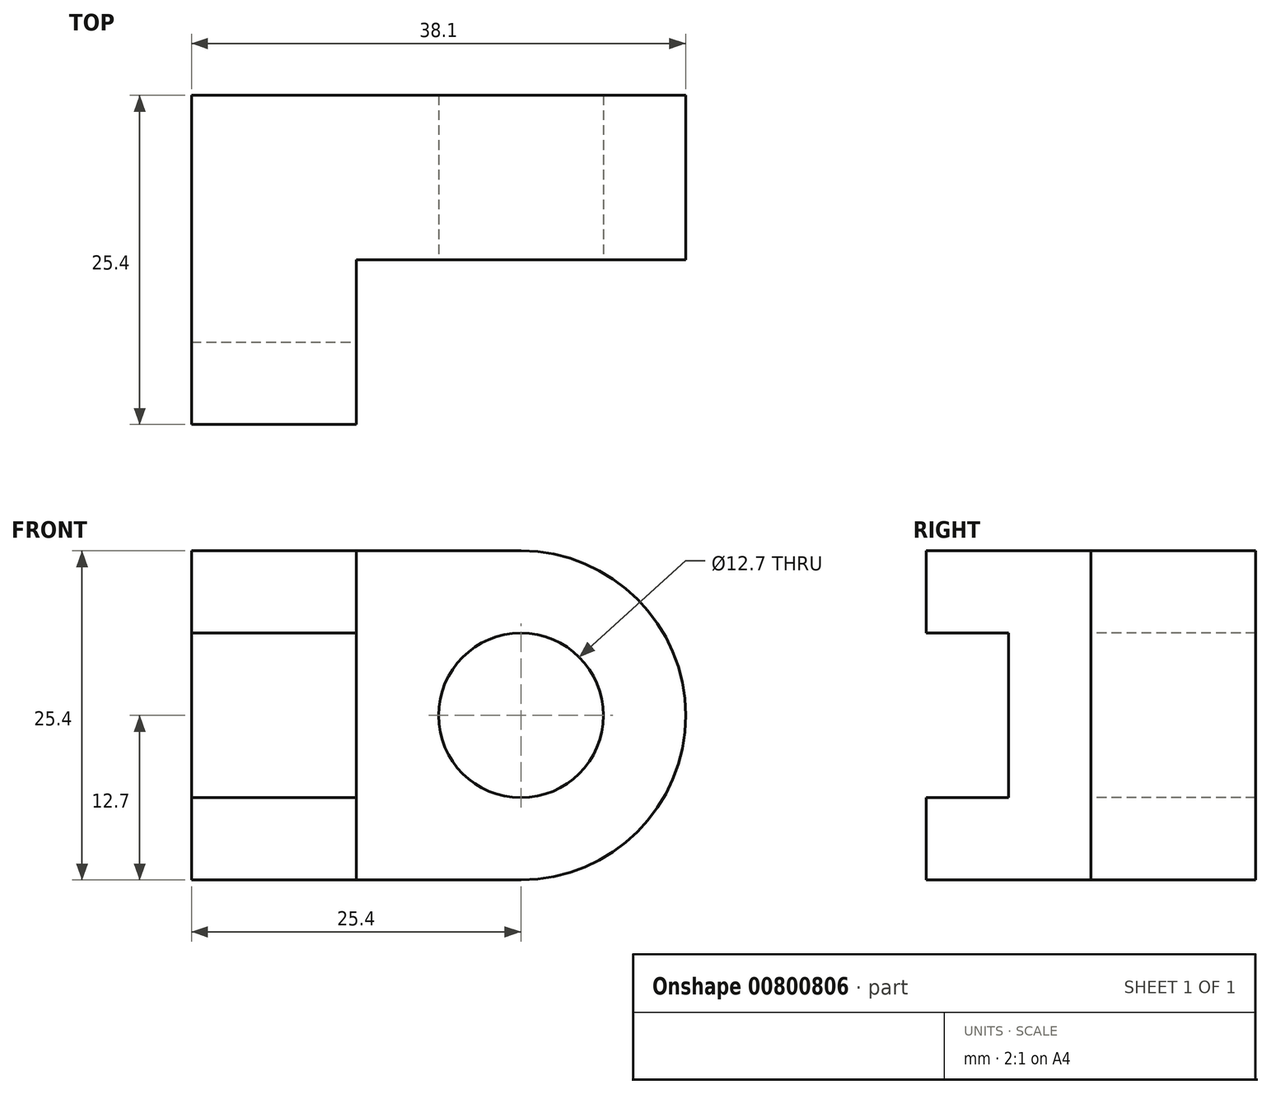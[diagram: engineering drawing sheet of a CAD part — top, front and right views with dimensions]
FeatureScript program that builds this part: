
annotation { "Feature Type Name" : "Feature", "Feature Type Description" : "" }
export const myFeature = defineFeature(function(context is Context, id is Id, definition is map)
    precondition{}
    {
        {
            var Q0;
            Q0=qCreatedBy(makeId("Top.planeOp"),FACE);
            var sketch = newSketch(context, id + "F0", { "sketchPlane" : qUnion([Q0])});
            skLineSegment(sketch, "E0", {"start": v(0, 0) * mm, "end": v(0, -25.4) * mm});
            skLineSegment(sketch, "E1", {"start": v(0, -25.4) * mm, "end": v(12.7, -25.4) * mm});
            skLineSegment(sketch, "E2", {"start": v(12.7, -25.4) * mm, "end": v(12.7, -12.7) * mm});
            skLineSegment(sketch, "E3", {"start": v(12.7, -12.7) * mm, "end": v(50.8, -12.7) * mm});
            skLineSegment(sketch, "E4", {"start": v(50.8, -12.7) * mm, "end": v(50.8, 0) * mm});
            skLineSegment(sketch, "E5", {"start": v(50.8, 0) * mm, "end": v(0, 0) * mm});
            skSolve(sketch);
        }
        {
            var Q0;
            Q0 = qSketchRegion(id + "F0", true);
            extrude(context, id + "F1", {"entities" : qUnion([Q0]), "oppositeDirection" : true, "depth" : 25.4 * mm, "offsetDistance" : 25.4 * mm});
        }
        {
            var Q0;
            Q0=makeQuery(id+"F1.opExtrude","SWEPT_FACE",FACE,{"disambiguationData":[OSD([sQuery(id+"F0.wireOp",EDGE,"E2")])]});
            var sketch = newSketch(context, id + "F2", { "sketchPlane" : qUnion([Q0])});
            skLineSegment(sketch, "E6", {"start": v(-25.4, 0) * mm, "end": v(-25.4, -6.35) * mm});
            skLineSegment(sketch, "E7", {"start": v(-25.4, -6.35) * mm, "end": v(-19.05, -6.35) * mm});
            skLineSegment(sketch, "E8", {"start": v(-19.05, -6.35) * mm, "end": v(-19.05, -19.05) * mm});
            skLineSegment(sketch, "E9", {"start": v(-19.05, -19.05) * mm, "end": v(-25.4, -19.05) * mm});
            skLineSegment(sketch, "E10", {"start": v(-25.4, -19.05) * mm, "end": v(-25.4, -25.4) * mm});
            skLineSegment(sketch, "E11", {"start": v(-25.4, -25.4) * mm, "end": v(-12.7, -25.4) * mm});
            skLineSegment(sketch, "E12", {"start": v(-12.7, -25.4) * mm, "end": v(-12.7, 0) * mm});
            skLineSegment(sketch, "E13", {"start": v(-12.7, 0) * mm, "end": v(-25.4, 0) * mm});
            skSolve(sketch);
        }
        {
            var Q0;
            {var subQ0=sQuery(id+"F2.wireOp",EDGE,"E7");Q0=makeQuery(id+"F2.imprint","IMPRINT",FACE,{"disambiguationData":[TD([[makeQuery(id+"F2.imprint","IMPRINT",EDGE,{"derivedFrom":subQ0}),-1.0]])]});}
            extrude(context, id + "F3", {"entities" : qUnion([Q0]), "operationType" : NewBodyOperationType.REMOVE, "oppositeDirection" : true, "depth" : 12.7 * mm, "offsetDistance" : 25.4 * mm});
        }
        {
            var Q0;
            Q0=makeQuery(id+"F1.opExtrude","SWEPT_FACE",FACE,{"disambiguationData":[OSD([sQuery(id+"F0.wireOp",EDGE,"E3")])]});
            var sketch = newSketch(context, id + "F4", { "sketchPlane" : qUnion([Q0])});
            skArc(sketch, "E14", {"start": v(25.4, -25.4) * mm, "mid": v(38.1, -12.7) * mm, "end": v(25.4, 0) * mm});
            skSolve(sketch);
        }
        {
            var Q0;
            {var subQ0=sQuery(id+"F4.wireOp",EDGE,"E14");Q0=makeQuery(id+"F4.imprint","IMPRINT",FACE,{"disambiguationData":[TD([[makeQuery(id+"F4.imprint","IMPRINT",EDGE,{"derivedFrom":subQ0}),-1.0]])]});}
            extrude(context, id + "F5", {"entities" : qUnion([Q0]), "operationType" : NewBodyOperationType.REMOVE, "oppositeDirection" : true, "depth" : 12.7 * mm, "offsetDistance" : 25.4 * mm});
        }
        {
            var Q0;
            Q0=makeQuery(id+"F1.opExtrude","SWEPT_FACE",FACE,{"disambiguationData":[OSD([sQuery(id+"F0.wireOp",EDGE,"E3")])]});
            var sketch = newSketch(context, id + "F6", { "sketchPlane" : qUnion([Q0])});
            skCircle(sketch, "E15", {"center": v(25.4, -12.7) * mm, "radius": 6.35 * mm});
            skSolve(sketch);
        }
        {
            var Q0;
            Q0=makeQuery(id+"F6.imprint","IMPRINT",FACE,{"disambiguationData":[TD([[makeQuery(id+"F6.imprint","IMPRINT",EDGE,{"derivedFrom":sQuery(id+"F6.wireOp",EDGE,"E15")}),1.0]])]});
            extrude(context, id + "F7", {"entities" : qUnion([Q0]), "operationType" : NewBodyOperationType.REMOVE, "oppositeDirection" : true, "depth" : 12.7 * mm, "offsetDistance" : 25.4 * mm});
        }
    });
